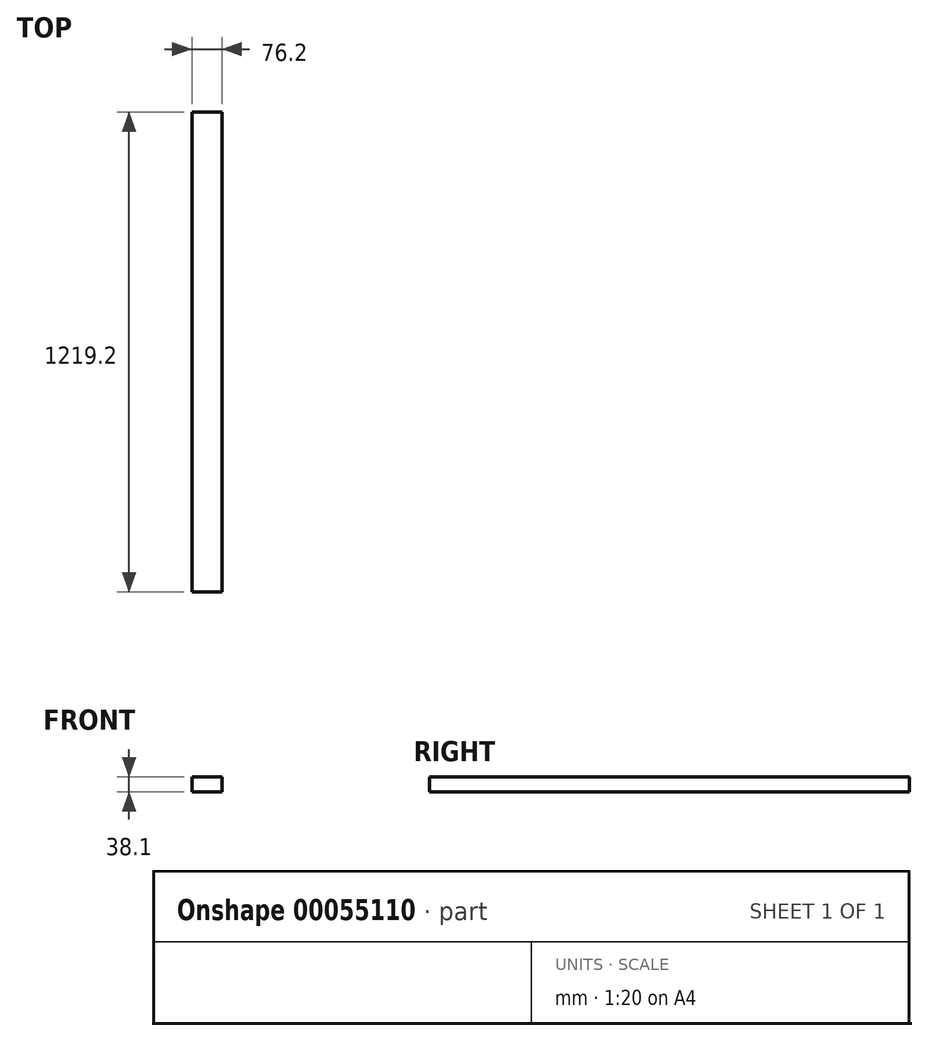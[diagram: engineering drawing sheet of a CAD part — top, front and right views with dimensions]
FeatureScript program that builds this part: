
annotation { "Feature Type Name" : "Feature", "Feature Type Description" : "" }
export const myFeature = defineFeature(function(context is Context, id is Id, definition is map)
    precondition{}
    {
        {
            var Q0;
            Q0=qCreatedBy(makeId("Front.planeOp"),FACE);
            var sketch = newSketch(context, id + "F0", { "sketchPlane" : qUnion([Q0])});
            skLineSegment(sketch, "E0.bottom", {"start": v(-38.1, -19.05) * mm, "end": v(38.1, -19.05) * mm});
            skLineSegment(sketch, "E0.top", {"start": v(-38.1, 19.05) * mm, "end": v(38.1, 19.05) * mm});
            skLineSegment(sketch, "E0.left", {"start": v(-38.1, -19.05) * mm, "end": v(-38.1, 19.05) * mm});
            skLineSegment(sketch, "E0.right", {"start": v(38.1, -19.05) * mm, "end": v(38.1, 19.05) * mm});
            skLineSegment(sketch, "E1", {"start": v(-38.1, 19.05) * mm, "end": v(0, 0) * mm, "construction": true});
            skLineSegment(sketch, "E2", {"start": v(0, 0) * mm, "end": v(38.1, -19.05) * mm, "construction": true});
            skSolve(sketch);
        }
        {
            var Q0;
            Q0 = qSketchRegion(id + "F0", true);
            extrude(context, id + "F1", {"entities" : qUnion([Q0]), "depth" : 1219.2 * mm});
        }
    });
